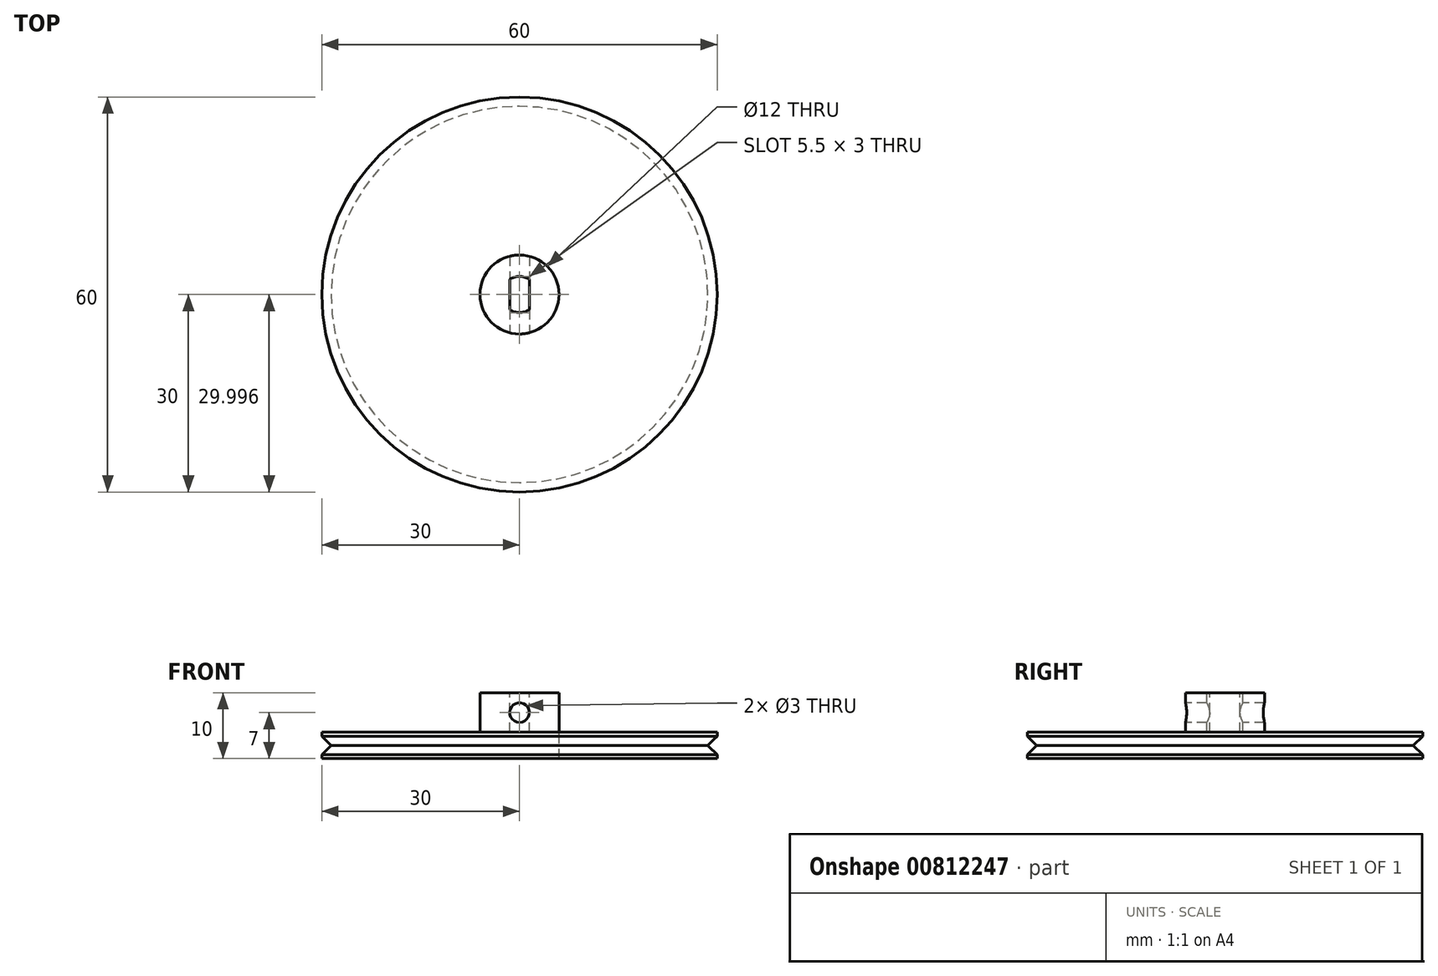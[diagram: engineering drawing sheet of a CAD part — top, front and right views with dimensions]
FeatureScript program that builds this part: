
annotation { "Feature Type Name" : "Feature", "Feature Type Description" : "" }
export const myFeature = defineFeature(function(context is Context, id is Id, definition is map)
    precondition{}
    {
        {
            var Q0;
            Q0=qCreatedBy(makeId("Top.planeOp"),FACE);
            var sketch = newSketch(context, id + "F0", { "sketchPlane" : qUnion([Q0])});
            skCircle(sketch, "E0", {"center": v(0, 0) * mm, "radius": 30 * mm});
            skCircle(sketch, "E1", {"center": v(0, 0) * mm, "radius": 6 * mm});
            skSolve(sketch);
        }
        {
            var Q0;
            Q0=makeQuery(id+"F0.imprint","IMPRINT",FACE,{"disambiguationData":[TD([[makeQuery(id+"F0.imprint","IMPRINT",EDGE,{"derivedFrom":sQuery(id+"F0.wireOp",EDGE,"E0")}),1.0]])]});
            extrude(context, id + "F1", {"entities" : qUnion([Q0]), "oppositeDirection" : true, "depth" : 4 * mm, "offsetDistance" : 25 * mm});
        }
        {
            var Q0;
            Q0=makeQuery(id+"F0.imprint","IMPRINT",FACE,{"disambiguationData":[TD([[makeQuery(id+"F0.imprint","IMPRINT",EDGE,{"derivedFrom":sQuery(id+"F0.wireOp",EDGE,"E1")}),1.0]])]});
            extrude(context, id + "F2", {"entities" : qUnion([Q0]), "depth" : 6 * mm, "offsetDistance" : 25 * mm});
        }
        {
            var Q0;
            Q0=qCreatedBy(makeId("Front.planeOp"),FACE);
            var sketch = newSketch(context, id + "F3", { "sketchPlane" : qUnion([Q0])});
            skCircle(sketch, "E2", {"center": v(0, 3) * mm, "radius": 1.5 * mm});
            skSolve(sketch);
        }
        {
            var Q0;
            Q0 = qSketchRegion(id + "F3", true);
            extrude(context, id + "F4", {"entities" : qUnion([Q0]), "operationType" : NewBodyOperationType.REMOVE, "endBound" : BoundingType.SYMMETRIC, "oppositeDirection" : true, "depth" : 25 * mm, "offsetDistance" : 25 * mm});
        }
        {
            var Q0;
            Q0=makeQuery(id+"F2.opExtrude","CAP_FACE",FACE,{"disambiguationData":[OSD([sQuery(id+"F0.wireOp",EDGE,"E1")])],"isStart":false});
            var sketch = newSketch(context, id + "F5", { "sketchPlane" : qUnion([Q0])});
            skLineSegment(sketch, "E3.bottom", {"start": v(-1.5, -2.3) * mm, "end": v(1.5, -2.3) * mm});
            skLineSegment(sketch, "E3.top", {"start": v(-1.5, 2.3) * mm, "end": v(1.5, 2.3) * mm});
            skLineSegment(sketch, "E3.left", {"start": v(-1.5, -2.3) * mm, "end": v(-1.5, 2.3) * mm});
            skLineSegment(sketch, "E3.right", {"start": v(1.5, -2.3) * mm, "end": v(1.5, 2.3) * mm});
            skPoint(sketch, "E3.middle", {"position": v(0, 0) * mm});
            skArc(sketch, "E4", {"start": v(1.5, 2.3) * mm, "mid": v(0, 2.75) * mm, "end": v(-1.5, 2.3) * mm});
            skArc(sketch, "E5", {"start": v(-1.5, -2.3) * mm, "mid": v(0, -2.75) * mm, "end": v(1.5, -2.3) * mm});
            skSolve(sketch);
        }
        {
            var Q0;
            Q0 = qSketchRegion(id + "F5", true);
            extrude(context, id + "F6", {"entities" : qUnion([Q0]), "operationType" : NewBodyOperationType.REMOVE, "oppositeDirection" : true, "depth" : 9.4 * mm, "offsetDistance" : 25 * mm});
        }
        {
            var Q0;
            Q0=qCreatedBy(makeId("Front.planeOp"),FACE);
            var sketch = newSketch(context, id + "F7", { "sketchPlane" : qUnion([Q0])});
            skLineSegment(sketch, "E6.0", {"start": v(-30, 0) * mm, "end": v(30, 0) * mm});
            skLineSegment(sketch, "E7", {"start": v(30, 0) * mm, "end": v(30, -4) * mm});
            skLineSegment(sketch, "E8", {"start": v(-30, -4) * mm, "end": v(-30, 0) * mm});
            skLineSegment(sketch, "E9", {"start": v(-30, -0.59) * mm, "end": v(-28.59, -2) * mm});
            skLineSegment(sketch, "E10", {"start": v(-28.59, -2) * mm, "end": v(-30, -3.41) * mm});
            skLineSegment(sketch, "E11", {"start": v(-30, -2) * mm, "end": v(-21.36, -2) * mm, "construction": true});
            skPoint(sketch, "E11.endSnap0", {"position": v(-30, -2) * mm});
            skLineSegment(sketch, "E12", {"start": v(0, 10.47) * mm, "end": v(0, -7.56) * mm, "construction": true});
            skSolve(sketch);
        }
        {
            var Q0;
            Q0 = qSketchRegion(id + "F7", true);
            var Q1;
            Q1=sQuery(id+"F7.wireOp",EDGE,"E9");
            var Q2;
            Q2=sQuery(id+"F7.wireOp",EDGE,"E10");
            var Q3;
            Q3=sQuery(id+"F7.wireOp",EDGE,"E12");
            revolve(context, id + "F8", {"operationType" : NewBodyOperationType.REMOVE, "surfaceOperationType" : NewSurfaceOperationType.NEW, "entities" : qUnion([Q0]), "surfaceEntities" : qUnion([Q1, Q2]), "axis" : qUnion([Q3]), "revolveType" : RevolveType.FULL});
        }
    });
